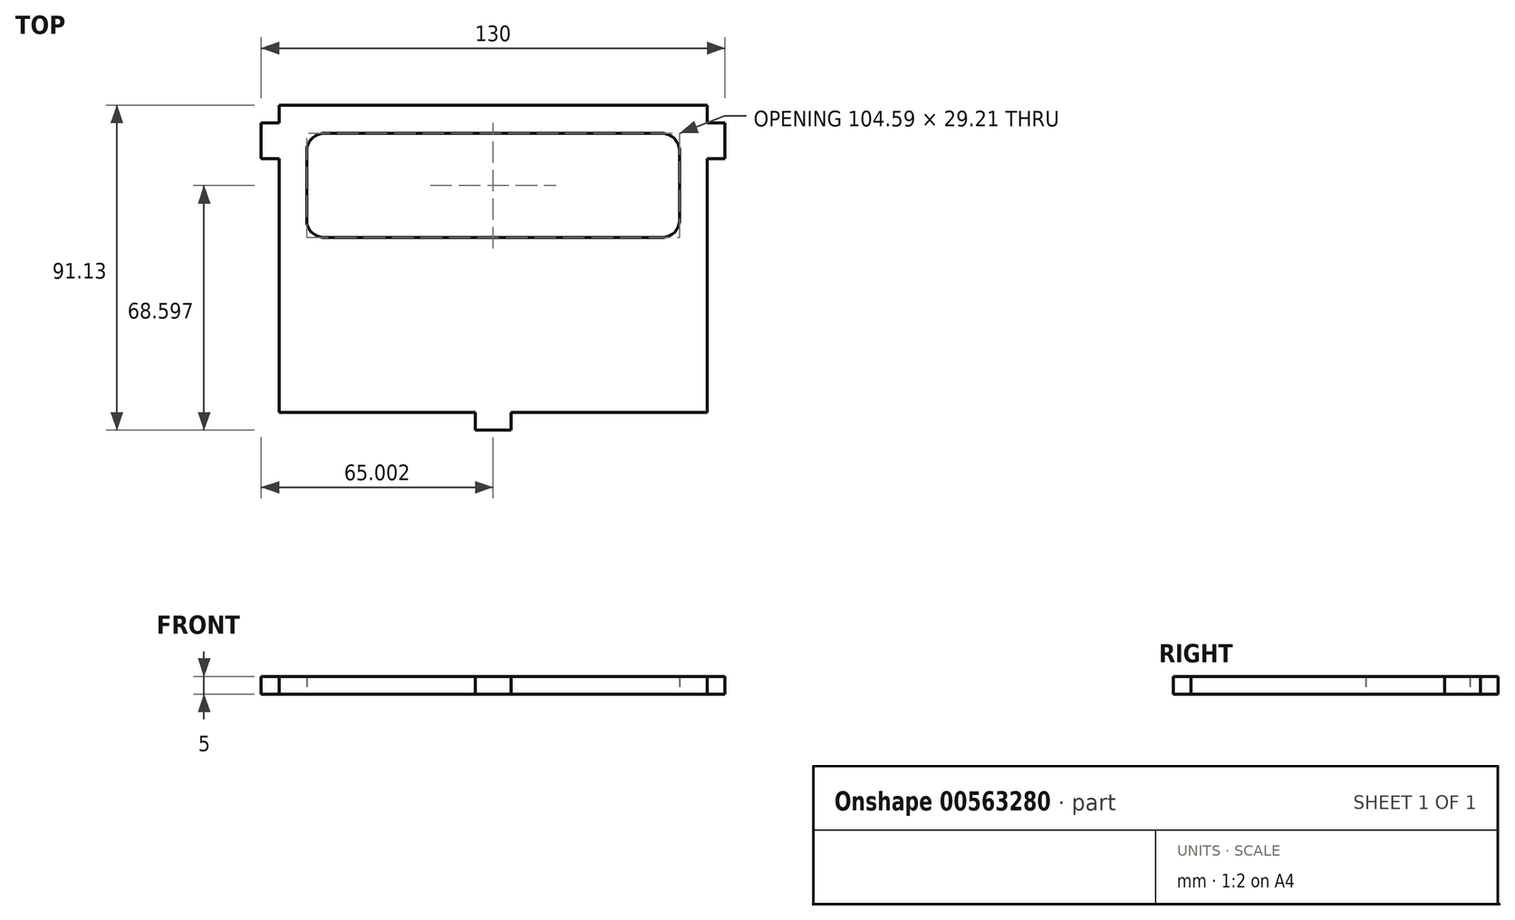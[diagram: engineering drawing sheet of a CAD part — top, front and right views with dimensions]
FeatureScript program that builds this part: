
annotation { "Feature Type Name" : "Feature", "Feature Type Description" : "" }
export const myFeature = defineFeature(function(context is Context, id is Id, definition is map)
    precondition{}
    {
        {
            var Q0;
            Q0=qCreatedBy(makeId("Top.planeOp"),FACE);
            var sketch = newSketch(context, id + "F0", { "sketchPlane" : qUnion([Q0])});
            skLineSegment(sketch, "E0.top", {"start": v(-2.52, -37.14) * mm, "end": v(47.48, -37.14) * mm});
            skLineSegment(sketch, "E0.left", {"start": v(-67.52, 49) * mm, "end": v(-67.52, 44) * mm});
            skLineSegment(sketch, "E0.right", {"start": v(52.48, 49) * mm, "end": v(52.48, 44) * mm});
            skLineSegment(sketch, "E1.bottom", {"start": v(-67.52, 44) * mm, "end": v(-72.52, 44) * mm});
            skLineSegment(sketch, "E1.top", {"start": v(-67.52, 34) * mm, "end": v(-72.52, 34) * mm});
            skLineSegment(sketch, "E1.right", {"start": v(-72.52, 44) * mm, "end": v(-72.52, 34) * mm});
            skLineSegment(sketch, "E2.bottom", {"start": v(52.48, 34) * mm, "end": v(57.48, 34) * mm});
            skLineSegment(sketch, "E2.top", {"start": v(52.48, 44) * mm, "end": v(57.48, 44) * mm});
            skLineSegment(sketch, "E2.right", {"start": v(57.48, 34) * mm, "end": v(57.48, 44) * mm});
            skLineSegment(sketch, "E3.trimOffspring", {"start": v(-67.52, 34) * mm, "end": v(-67.52, 20.92) * mm});
            skLineSegment(sketch, "E4.trimOffspring", {"start": v(52.48, 34) * mm, "end": v(52.48, 20.92) * mm});
            skLineSegment(sketch, "E5.top", {"start": v(-67.52, 49) * mm, "end": v(52.48, 49) * mm});
            skPoint(sketch, "E6.orphan", {"position": v(52.48, 54) * mm});
            skLineSegment(sketch, "E7", {"start": v(-62.52, -37.14) * mm, "end": v(-12.52, -37.14) * mm});
            skLineSegment(sketch, "E8.top", {"start": v(-12.52, -42.14) * mm, "end": v(-2.52, -42.14) * mm});
            skLineSegment(sketch, "E8.left", {"start": v(-12.52, -37.14) * mm, "end": v(-12.52, -42.14) * mm});
            skLineSegment(sketch, "E8.right", {"start": v(-2.52, -37.14) * mm, "end": v(-2.52, -42.14) * mm});
            skLineSegment(sketch, "E9.top", {"start": v(-67.52, -37.14) * mm, "end": v(-62.52, -37.14) * mm});
            skLineSegment(sketch, "E9.left", {"start": v(-67.52, 20.92) * mm, "end": v(-67.52, -37.14) * mm});
            skLineSegment(sketch, "E10.top", {"start": v(47.48, -37.14) * mm, "end": v(52.48, -37.14) * mm});
            skLineSegment(sketch, "E10.right", {"start": v(52.48, 20.92) * mm, "end": v(52.48, -37.14) * mm});
            skPoint(sketch, "E10.bottom.start.orphan", {"position": v(47.48, 20.92) * mm});
            skLineSegment(sketch, "E11.bottom", {"start": v(-54.81, 41.06) * mm, "end": v(39.78, 41.06) * mm});
            skLineSegment(sketch, "E11.top", {"start": v(-54.81, 11.85) * mm, "end": v(39.78, 11.85) * mm});
            skLineSegment(sketch, "E11.left", {"start": v(-59.81, 36.06) * mm, "end": v(-59.81, 16.85) * mm});
            skLineSegment(sketch, "E11.right", {"start": v(44.78, 36.06) * mm, "end": v(44.78, 16.85) * mm});
            skPoint(sketch, "E11.middle", {"position": v(-7.52, 26.46) * mm});
            skPoint(sketch, "E11.middle.positionSnap0", {"position": v(-7.52, 49) * mm});
            skPoint(sketch, "E11.centerSnap0", {"position": v(-7.52, 49) * mm});
            skPoint(sketch, "E12.visualSharp", {"position": v(-59.81, 41.06) * mm});
            skArc(sketch, "E12.filletArc", {"start": v(-54.81, 41.06) * mm, "mid": v(-58.35, 39.6) * mm, "end": v(-59.81, 36.06) * mm});
            skPoint(sketch, "E13.visualSharp", {"position": v(-59.81, 11.85) * mm});
            skArc(sketch, "E13.filletArc", {"start": v(-59.81, 16.85) * mm, "mid": v(-58.35, 13.32) * mm, "end": v(-54.81, 11.85) * mm});
            skPoint(sketch, "E14.visualSharp", {"position": v(44.78, 11.85) * mm});
            skArc(sketch, "E14.filletArc", {"start": v(39.78, 11.85) * mm, "mid": v(43.31, 13.32) * mm, "end": v(44.78, 16.85) * mm});
            skPoint(sketch, "E15.visualSharp", {"position": v(44.78, 41.06) * mm});
            skArc(sketch, "E15.filletArc", {"start": v(44.78, 36.06) * mm, "mid": v(43.31, 39.6) * mm, "end": v(39.78, 41.06) * mm});
            skSolve(sketch);
        }
        {
            var Q0;
            Q0 = qSketchRegion(id + "F0", true);
            extrude(context, id + "F1", {"entities" : qUnion([Q0]), "depth" : 5 * mm, "offsetDistance" : 25 * mm});
        }
    });
